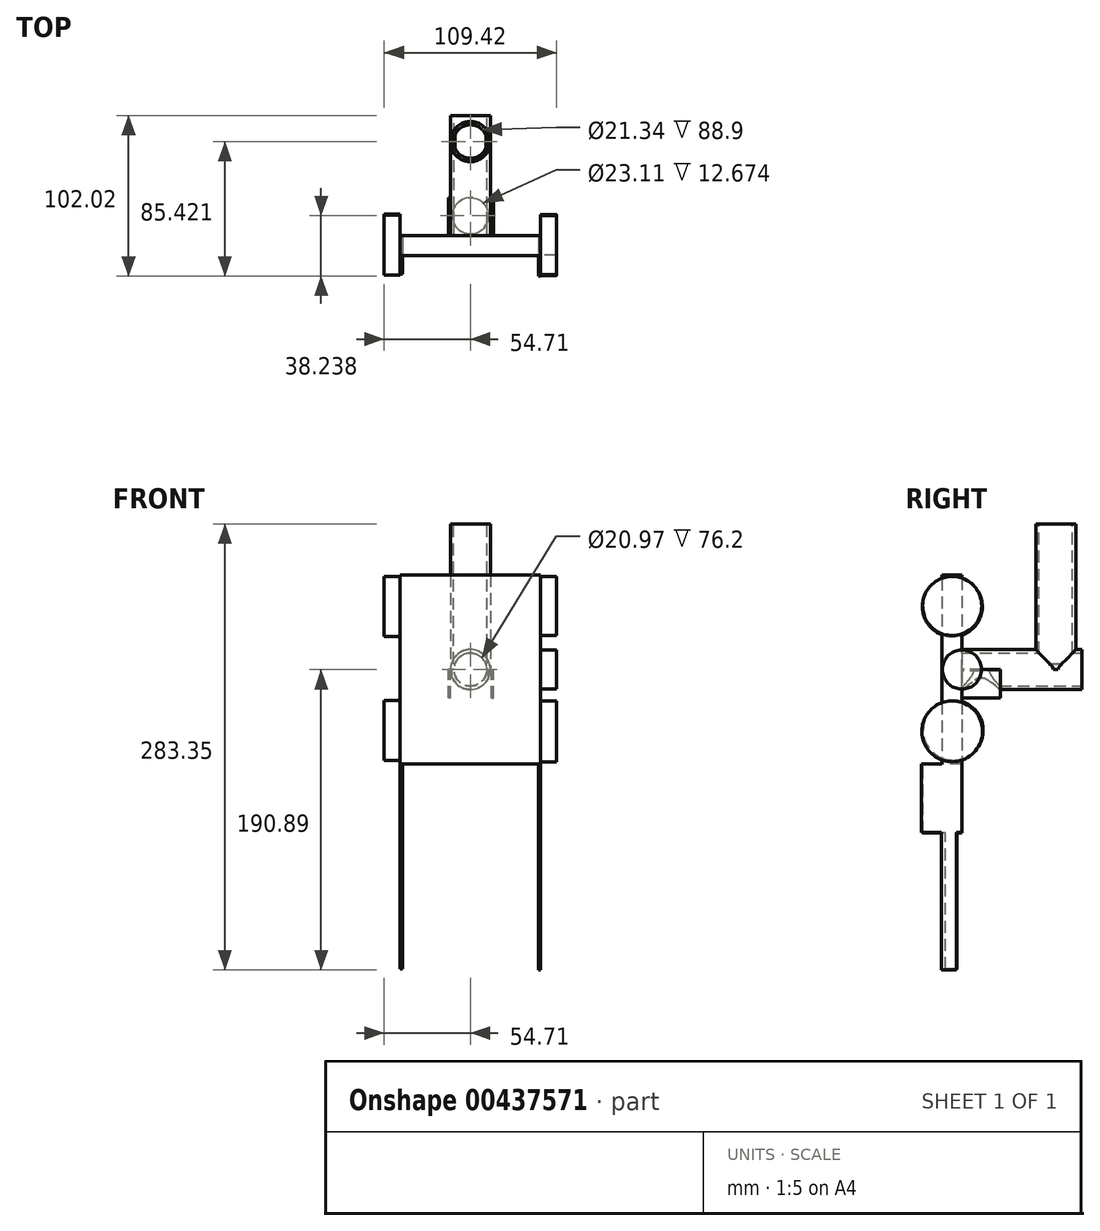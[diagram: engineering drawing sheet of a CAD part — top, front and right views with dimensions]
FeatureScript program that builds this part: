
annotation { "Feature Type Name" : "Feature", "Feature Type Description" : "" }
export const myFeature = defineFeature(function(context is Context, id is Id, definition is map)
    precondition{}
    {
        {
            var Q0;
            Q0=qCreatedBy(makeId("Front.planeOp"),FACE);
            var sketch = newSketch(context, id + "F0", { "sketchPlane" : qUnion([Q0])});
            skLineSegment(sketch, "E0.bottom", {"start": v(-44.55, 60.08) * mm, "end": v(44.55, 60.08) * mm});
            skLineSegment(sketch, "E0.top", {"start": v(-44.55, -60.08) * mm, "end": v(44.55, -60.08) * mm});
            skLineSegment(sketch, "E0.left", {"start": v(-44.55, 60.08) * mm, "end": v(-44.55, -60.08) * mm});
            skLineSegment(sketch, "E0.right", {"start": v(44.55, 60.08) * mm, "end": v(44.55, -60.08) * mm});
            skPoint(sketch, "E0.middle", {"position": v(0, 0) * mm});
            skSolve(sketch);
        }
        {
            var Q0;
            Q0 = qSketchRegion(id + "F0", true);
            extrude(context, id + "F1", {"entities" : qUnion([Q0]), "depth" : 12.7 * mm});
        }
        {
            var Q0;
            Q0=makeQuery(id+"F1.opExtrude","SWEPT_FACE",FACE,{"disambiguationData":[OSD([sQuery(id+"F0.wireOp",EDGE,"E0.left")])]});
            var sketch = newSketch(context, id + "F2", { "sketchPlane" : qUnion([Q0])});
            skCircle(sketch, "E1", {"center": v(6.09, 39.93) * mm, "radius": 19.05 * mm});
            skSolve(sketch);
        }
        {
            var Q0;
            Q0 = qSketchRegion(id + "F2", true);
            extrude(context, id + "F3", {"entities" : qUnion([Q0]), "operationType" : NewBodyOperationType.ADD, "depth" : 10.16 * mm});
        }
        {
            var Q0;
            {var subQ2=sQuery(id+"F0.wireOp",EDGE,"E0.left");var subQ3=sQuery(id+"F0.wireOp",EDGE,"E0.top");Q0=makeQuery(id+"F3.boolean.opBoolean","SPLIT",FACE,{"disambiguationData":[TD([makeQuery(id+"F1.opExtrude","SWEPT_FACE",FACE,{"disambiguationData":[OSD([subQ3])]})])],"derivedFrom":makeQuery(id+"F1.opExtrude","SWEPT_FACE",FACE,{"disambiguationData":[OSD([subQ2])]})});}
            var sketch = newSketch(context, id + "F4", { "sketchPlane" : qUnion([Q0])});
            skCircle(sketch, "E2", {"center": v(5.6, -38.55) * mm, "radius": 19.05 * mm});
            skSolve(sketch);
        }
        {
            var Q0;
            Q0 = qSketchRegion(id + "F4", true);
            extrude(context, id + "F5", {"entities" : qUnion([Q0]), "operationType" : NewBodyOperationType.ADD, "depth" : 10.16 * mm});
        }
        {
            var Q0;
            Q0=makeQuery(id+"F1.opExtrude","SWEPT_FACE",FACE,{"disambiguationData":[OSD([sQuery(id+"F0.wireOp",EDGE,"E0.right")])]});
            var sketch = newSketch(context, id + "F6", { "sketchPlane" : qUnion([Q0])});
            skCircle(sketch, "E3", {"center": v(-6.19, 40.36) * mm, "radius": 18.77 * mm});
            skSolve(sketch);
        }
        {
            var Q0;
            Q0 = qSketchRegion(id + "F6", true);
            extrude(context, id + "F7", {"entities" : qUnion([Q0]), "operationType" : NewBodyOperationType.ADD, "depth" : 10.16 * mm});
        }
        {
            var Q0;
            {var subQ0=sQuery(id+"F0.wireOp",EDGE,"E0.top");var subQ1=sQuery(id+"F0.wireOp",EDGE,"E0.right");Q0=makeQuery(id+"F7.boolean.opBoolean","SPLIT",FACE,{"disambiguationData":[TD([makeQuery(id+"F1.opExtrude","SWEPT_FACE",FACE,{"disambiguationData":[OSD([subQ0])]})])],"derivedFrom":makeQuery(id+"F1.opExtrude","SWEPT_FACE",FACE,{"disambiguationData":[OSD([subQ1])]})});}
            var sketch = newSketch(context, id + "F8", { "sketchPlane" : qUnion([Q0])});
            skCircle(sketch, "E4", {"center": v(-6.19, -39.23) * mm, "radius": 19.3 * mm});
            skSolve(sketch);
        }
        {
            var Q0;
            Q0 = qSketchRegion(id + "F8", true);
            extrude(context, id + "F9", {"entities" : qUnion([Q0]), "operationType" : NewBodyOperationType.ADD, "depth" : 10.16 * mm});
        }
        {
            var Q0;
            {var subQ0=sQuery(id+"F6.wireOp",EDGE,"E3");var subQ2=sQuery(id+"F0.wireOp",EDGE,"E0.right");var subQ4=sQuery(id+"F0.wireOp",EDGE,"E0.top");var subQ8=makeQuery(id+"F7.opExtrude","SWEPT_FACE",FACE,{"disambiguationData":[OSD([subQ0])]});Q0=makeQuery(id+"F9.boolean.opBoolean","SPLIT",FACE,{"disambiguationData":[TD([subQ8])],"derivedFrom":makeQuery(id+"F7.boolean.opBoolean","SPLIT",FACE,{"disambiguationData":[TD([makeQuery(id+"F1.opExtrude","SWEPT_FACE",FACE,{"disambiguationData":[OSD([subQ4])]})])],"derivedFrom":makeQuery(id+"F1.opExtrude","SWEPT_FACE",FACE,{"disambiguationData":[OSD([subQ2])]})})});}
            var sketch = newSketch(context, id + "F10", { "sketchPlane" : qUnion([Q0])});
            skCircle(sketch, "E5", {"center": v(0, 0) * mm, "radius": 12.42 * mm});
            skSolve(sketch);
        }
        {
            var Q0;
            Q0 = qSketchRegion(id + "F10", true);
            extrude(context, id + "F11", {"entities" : qUnion([Q0]), "operationType" : NewBodyOperationType.ADD, "depth" : 10.16 * mm});
        }
        {
            var Q0;
            Q0=makeQuery(id+"F1.opExtrude","CAP_FACE",FACE,{"disambiguationData":[OSD([sQuery(id+"F0.wireOp",EDGE,"E0.bottom"),sQuery(id+"F0.wireOp",EDGE,"E0.top"),sQuery(id+"F0.wireOp",EDGE,"E0.left"),sQuery(id+"F0.wireOp",EDGE,"E0.right")])],"isStart":true});
            var sketch = newSketch(context, id + "F12", { "sketchPlane" : qUnion([Q0])});
            skCircle(sketch, "E6", {"center": v(0, 0) * mm, "radius": 12.67 * mm});
            skSolve(sketch);
        }
        {
            var Q0;
            Q0 = qSketchRegion(id + "F12", true);
            extrude(context, id + "F13", {"entities" : qUnion([Q0]), "operationType" : NewBodyOperationType.ADD, "depth" : 76.2 * mm});
        }
        {
            var Q0;
            Q0=qCreatedBy(makeId("Top.planeOp"),FACE);
            var sketch = newSketch(context, id + "F14", { "sketchPlane" : qUnion([Q0])});
            skCircle(sketch, "E7", {"center": v(0, 59.6) * mm, "radius": 12.74 * mm});
            skSolve(sketch);
        }
        {
            var Q0;
            Q0 = qSketchRegion(id + "F14", true);
            extrude(context, id + "F15", {"entities" : qUnion([Q0]), "operationType" : NewBodyOperationType.ADD, "depth" : 92.46 * mm});
        }
        {
            var Q0;
            Q0=makeQuery(id+"F13.opExtrude","CAP_FACE",FACE,{"disambiguationData":[OSD([sQuery(id+"F12.wireOp",EDGE,"E6")])],"isStart":false});
            var sketch = newSketch(context, id + "F16", { "sketchPlane" : qUnion([Q0])});
            skCircle(sketch, "E8", {"center": v(0, 0) * mm, "radius": 10.49 * mm});
            skSolve(sketch);
        }
        {
            var Q0;
            Q0 = qSketchRegion(id + "F16", true);
            extrude(context, id + "F17", {"entities" : qUnion([Q0]), "operationType" : NewBodyOperationType.REMOVE, "oppositeDirection" : true, "depth" : 76.2 * mm});
        }
        {
            var Q0;
            Q0=makeQuery(id+"F15.opExtrude","CAP_FACE",FACE,{"disambiguationData":[OSD([sQuery(id+"F14.wireOp",EDGE,"E7")])],"isStart":false});
            var sketch = newSketch(context, id + "F18", { "sketchPlane" : qUnion([Q0])});
            skCircle(sketch, "E9", {"center": v(0, 59.6) * mm, "radius": 10.67 * mm});
            skSolve(sketch);
        }
        {
            var Q0;
            Q0 = qSketchRegion(id + "F18", true);
            extrude(context, id + "F19", {"entities" : qUnion([Q0]), "operationType" : NewBodyOperationType.REMOVE, "oppositeDirection" : true, "depth" : 88.9 * mm});
        }
        {
            var Q0;
            Q0=qCreatedBy(makeId("Top.planeOp"),FACE);
            var sketch = newSketch(context, id + "F20", { "sketchPlane" : qUnion([Q0])});
            skCircle(sketch, "E10", {"center": v(0, 12.42) * mm, "radius": 11.56 * mm});
            skSolve(sketch);
        }
        {
            var Q0;
            Q0 = qSketchRegion(id + "F20", true);
            extrude(context, id + "F21", {"entities" : qUnion([Q0]), "operationType" : NewBodyOperationType.REMOVE, "oppositeDirection" : true, "depth" : 25.4 * mm});
        }
        {
            var Q0;
            Q0=qCreatedBy(makeId("Top.planeOp"),FACE);
            var sketch = newSketch(context, id + "F22", { "sketchPlane" : qUnion([Q0])});
            skLineSegment(sketch, "E11.bottom", {"start": v(13.4, 24.43) * mm, "end": v(14.65, 24.43) * mm});
            skLineSegment(sketch, "E11.top", {"start": v(13.4, 0) * mm, "end": v(14.65, 0) * mm});
            skLineSegment(sketch, "E11.left", {"start": v(13.4, 24.43) * mm, "end": v(13.4, 0) * mm});
            skLineSegment(sketch, "E11.right", {"start": v(14.65, 24.43) * mm, "end": v(14.65, 0) * mm});
            skSolve(sketch);
        }
        {
            var Q0;
            Q0=qCreatedBy(makeId("Top.planeOp"),FACE);
            var sketch = newSketch(context, id + "F23", { "sketchPlane" : qUnion([Q0])});
            skLineSegment(sketch, "E12.bottom", {"start": v(-12.64, 24.1) * mm, "end": v(-13.94, 24.1) * mm});
            skLineSegment(sketch, "E12.top", {"start": v(-12.64, 0) * mm, "end": v(-13.94, 0) * mm});
            skLineSegment(sketch, "E12.left", {"start": v(-12.64, 24.1) * mm, "end": v(-12.64, 0) * mm});
            skLineSegment(sketch, "E12.right", {"start": v(-13.94, 24.1) * mm, "end": v(-13.94, 0) * mm});
            skSolve(sketch);
        }
        {
            var Q0;
            Q0=makeQuery(id+"F1.opExtrude","SWEPT_FACE",FACE,{"disambiguationData":[OSD([sQuery(id+"F0.wireOp",EDGE,"E0.top")])]});
            var sketch = newSketch(context, id + "F24", { "sketchPlane" : qUnion([Q0])});
            skLineSegment(sketch, "E13.bottom", {"start": v(44.55, 0) * mm, "end": v(43.23, 0) * mm});
            skLineSegment(sketch, "E13.top", {"start": v(44.55, 25.82) * mm, "end": v(43.23, 25.82) * mm});
            skLineSegment(sketch, "E13.left", {"start": v(44.55, 0) * mm, "end": v(44.55, 25.82) * mm});
            skLineSegment(sketch, "E13.right", {"start": v(43.23, 0) * mm, "end": v(43.23, 25.82) * mm});
            skSolve(sketch);
        }
        {
            var Q0;
            Q0 = qSketchRegion(id + "F24", true);
            extrude(context, id + "F25", {"entities" : qUnion([Q0]), "operationType" : NewBodyOperationType.ADD, "depth" : 43.43 * mm});
        }
        {
            var Q0;
            Q0=makeQuery(id+"F1.opExtrude","SWEPT_FACE",FACE,{"disambiguationData":[OSD([sQuery(id+"F0.wireOp",EDGE,"E0.top")])]});
            var sketch = newSketch(context, id + "F26", { "sketchPlane" : qUnion([Q0])});
            skLineSegment(sketch, "E14.bottom", {"start": v(-44.55, 0) * mm, "end": v(-43.11, 0) * mm});
            skLineSegment(sketch, "E14.top", {"start": v(-44.55, 24.65) * mm, "end": v(-43.11, 24.65) * mm});
            skLineSegment(sketch, "E14.left", {"start": v(-44.55, 0) * mm, "end": v(-44.55, 24.65) * mm});
            skLineSegment(sketch, "E14.right", {"start": v(-43.11, 0) * mm, "end": v(-43.11, 24.65) * mm});
            skSolve(sketch);
        }
        {
            var Q0;
            Q0 = qSketchRegion(id + "F26", true);
            extrude(context, id + "F27", {"entities" : qUnion([Q0]), "operationType" : NewBodyOperationType.ADD, "depth" : 43.69 * mm});
        }
        {
            var Q0;
            Q0=makeQuery(id+"F27.opExtrude","SWEPT_FACE",FACE,{"disambiguationData":[OSD([sQuery(id+"F26.wireOp",EDGE,"E14.right")])]});
            var sketch = newSketch(context, id + "F28", { "sketchPlane" : qUnion([Q0])});
            skLineSegment(sketch, "E15", {"start": v(0, -60.08) * mm, "end": v(-24.65, -103.77) * mm});
            skSolve(sketch);
        }
        {
            var Q0;
            Q0=sQuery(id+"F28.wireOp",EDGE,"E15");
            extrude(context, id + "F29", {"bodyType" : ToolBodyType.SURFACE, "surfaceEntities" : qUnion([Q0]), "depth" : 86.36 * mm});
        }
        {
            var Q0;
            Q0 = qSketchRegion(id + "F22", true);
            extrude(context, id + "F30", {"entities" : qUnion([Q0]), "operationType" : NewBodyOperationType.ADD, "oppositeDirection" : true, "depth" : 18.03 * mm});
        }
        {
            var Q0;
            Q0 = qSketchRegion(id + "F23", true);
            extrude(context, id + "F31", {"entities" : qUnion([Q0]), "operationType" : NewBodyOperationType.ADD, "oppositeDirection" : true, "depth" : 18.03 * mm});
        }
        {
            var Q0;
            Q0=makeQuery(id+"F27.boolean.opBoolean","MERGE",FACE,{"derivedFrom":[makeQuery(id+"F25.boolean.opBoolean","MERGE",FACE,{"derivedFrom":[makeQuery(id+"F1.opExtrude","CAP_FACE",FACE,{"disambiguationData":[OSD([sQuery(id+"F0.wireOp",EDGE,"E0.bottom"),sQuery(id+"F0.wireOp",EDGE,"E0.top"),sQuery(id+"F0.wireOp",EDGE,"E0.left"),sQuery(id+"F0.wireOp",EDGE,"E0.right")])],"isStart":true}),makeQuery(id+"F25.opExtrude","SWEPT_FACE",FACE,{"disambiguationData":[OSD([sQuery(id+"F24.wireOp",EDGE,"E13.bottom")])]})]}),makeQuery(id+"F27.opExtrude","SWEPT_FACE",FACE,{"disambiguationData":[OSD([sQuery(id+"F26.wireOp",EDGE,"E14.bottom")])]})]});
            var sketch = newSketch(context, id + "F32", { "sketchPlane" : qUnion([Q0])});
            skLineSegment(sketch, "E16", {"start": v(13.94, -18.03) * mm, "end": v(43.11, -60.08) * mm});
            skSolve(sketch);
        }
        {
            var Q0;
            Q0=sQuery(id+"F32.wireOp",EDGE,"E16");
            extrude(context, id + "F33", {"bodyType" : ToolBodyType.SURFACE, "surfaceEntities" : qUnion([Q0]), "depth" : 23.88 * mm});
        }
        {
            var Q0;
            Q0=makeQuery(id+"F27.boolean.opBoolean","MERGE",FACE,{"derivedFrom":[makeQuery(id+"F25.boolean.opBoolean","MERGE",FACE,{"derivedFrom":[makeQuery(id+"F1.opExtrude","CAP_FACE",FACE,{"disambiguationData":[OSD([sQuery(id+"F0.wireOp",EDGE,"E0.bottom"),sQuery(id+"F0.wireOp",EDGE,"E0.top"),sQuery(id+"F0.wireOp",EDGE,"E0.left"),sQuery(id+"F0.wireOp",EDGE,"E0.right")])],"isStart":true}),makeQuery(id+"F25.opExtrude","SWEPT_FACE",FACE,{"disambiguationData":[OSD([sQuery(id+"F24.wireOp",EDGE,"E13.bottom")])]})]}),makeQuery(id+"F27.opExtrude","SWEPT_FACE",FACE,{"disambiguationData":[OSD([sQuery(id+"F26.wireOp",EDGE,"E14.bottom")])]})]});
            var sketch = newSketch(context, id + "F34", { "sketchPlane" : qUnion([Q0])});
            skLineSegment(sketch, "E17", {"start": v(-14.65, -18.03) * mm, "end": v(-43.23, -60.08) * mm});
            skSolve(sketch);
        }
        {
            var Q0;
            Q0=sQuery(id+"F34.wireOp",EDGE,"E17");
            extrude(context, id + "F35", {"bodyType" : ToolBodyType.SURFACE, "surfaceEntities" : qUnion([Q0]), "depth" : 24.13 * mm});
        }
        {
            var Q0;
            Q0=makeQuery(id+"F25.opExtrude","CAP_FACE",FACE,{"disambiguationData":[OSD([sQuery(id+"F24.wireOp",EDGE,"E13.bottom"),sQuery(id+"F24.wireOp",EDGE,"E13.top"),sQuery(id+"F24.wireOp",EDGE,"E13.left"),sQuery(id+"F24.wireOp",EDGE,"E13.right")])],"isStart":false});
            var sketch = newSketch(context, id + "F36", { "sketchPlane" : qUnion([Q0])});
            skLineSegment(sketch, "E18.bottom", {"start": v(44.55, 3.37) * mm, "end": v(43.23, 3.37) * mm});
            skLineSegment(sketch, "E18.top", {"start": v(44.55, 12.91) * mm, "end": v(43.23, 12.91) * mm});
            skLineSegment(sketch, "E18.left", {"start": v(44.55, 3.37) * mm, "end": v(44.55, 12.91) * mm});
            skLineSegment(sketch, "E18.right", {"start": v(43.23, 3.37) * mm, "end": v(43.23, 12.91) * mm});
            skSolve(sketch);
        }
        {
            var Q0;
            Q0 = qSketchRegion(id + "F36", true);
            extrude(context, id + "F37", {"entities" : qUnion([Q0]), "operationType" : NewBodyOperationType.ADD, "depth" : 87.38 * mm});
        }
        {
            var Q0;
            Q0=makeQuery(id+"F27.opExtrude","CAP_FACE",FACE,{"disambiguationData":[OSD([sQuery(id+"F26.wireOp",EDGE,"E14.bottom"),sQuery(id+"F26.wireOp",EDGE,"E14.top"),sQuery(id+"F26.wireOp",EDGE,"E14.left"),sQuery(id+"F26.wireOp",EDGE,"E14.right")])],"isStart":false});
            var sketch = newSketch(context, id + "F38", { "sketchPlane" : qUnion([Q0])});
            skLineSegment(sketch, "E19.bottom", {"start": v(-43.11, 3.11) * mm, "end": v(-44.55, 3.11) * mm});
            skLineSegment(sketch, "E19.top", {"start": v(-43.11, 10.43) * mm, "end": v(-44.55, 10.43) * mm});
            skLineSegment(sketch, "E19.left", {"start": v(-43.11, 3.11) * mm, "end": v(-43.11, 10.43) * mm});
            skLineSegment(sketch, "E19.right", {"start": v(-44.55, 3.11) * mm, "end": v(-44.55, 10.43) * mm});
            skSolve(sketch);
        }
        {
            var Q0;
            Q0 = qSketchRegion(id + "F38", true);
            extrude(context, id + "F39", {"entities" : qUnion([Q0]), "operationType" : NewBodyOperationType.ADD, "depth" : 86.36 * mm});
        }
    });
